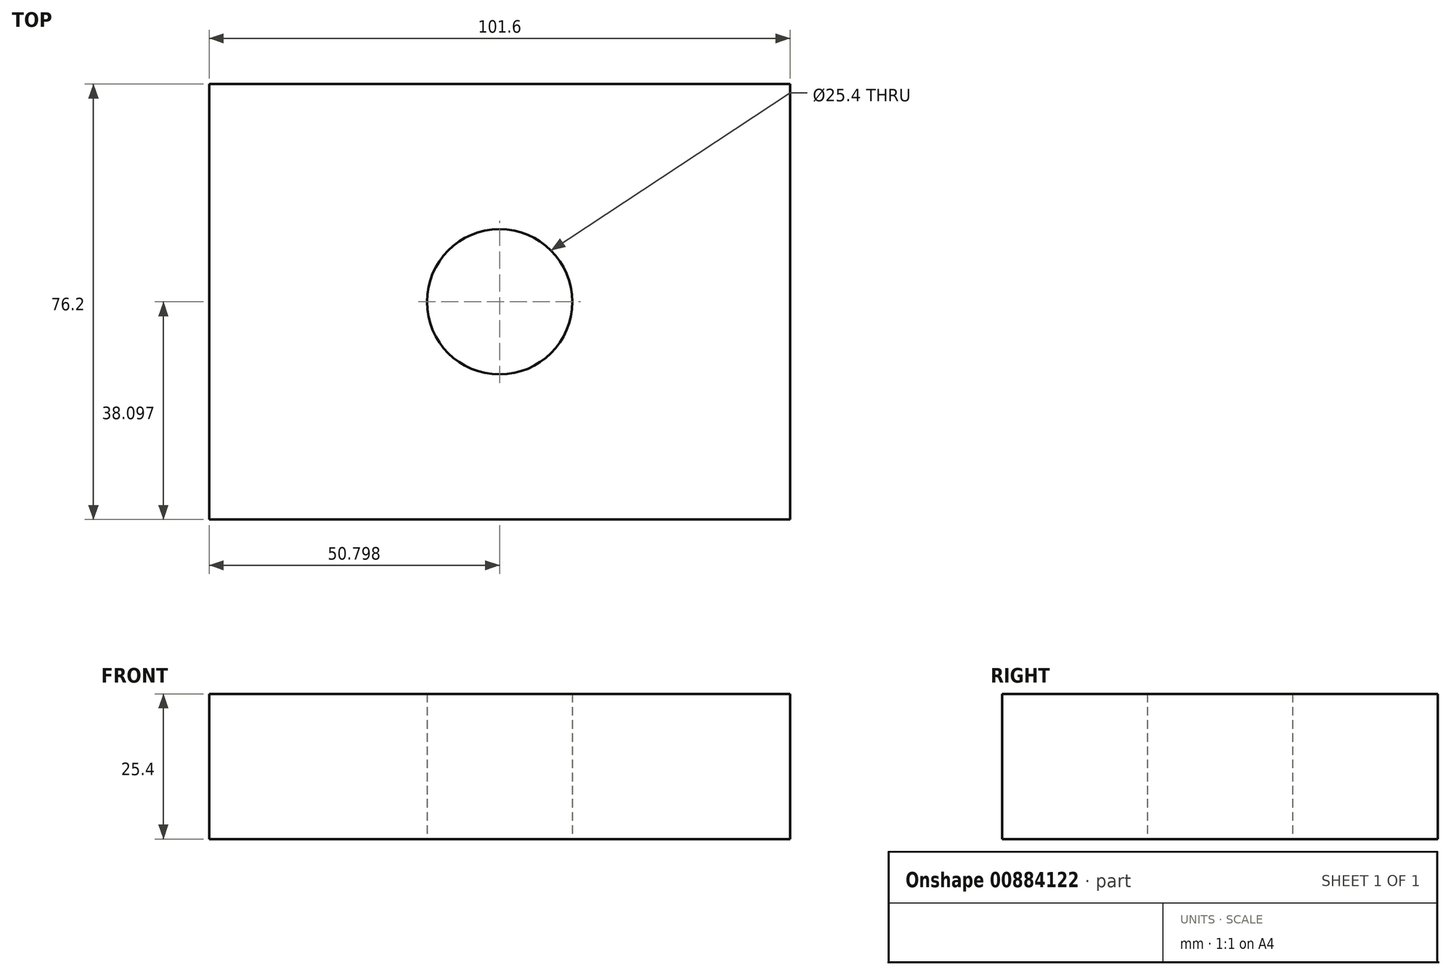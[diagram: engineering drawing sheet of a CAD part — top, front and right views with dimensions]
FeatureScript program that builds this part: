
annotation { "Feature Type Name" : "Feature", "Feature Type Description" : "" }
export const myFeature = defineFeature(function(context is Context, id is Id, definition is map)
    precondition{}
    {
        {
            var Q0;
            Q0=qCreatedBy(makeId("Top.planeOp"),FACE);
            var sketch = newSketch(context, id + "F0", { "sketchPlane" : qUnion([Q0])});
            skLineSegment(sketch, "E0.bottom", {"start": v(58.3, 44.06) * mm, "end": v(-43.3, 44.06) * mm});
            skLineSegment(sketch, "E0.top", {"start": v(58.3, -32.14) * mm, "end": v(-43.3, -32.14) * mm});
            skLineSegment(sketch, "E0.left", {"start": v(58.3, 44.06) * mm, "end": v(58.3, -32.14) * mm});
            skLineSegment(sketch, "E0.right", {"start": v(-43.3, 44.06) * mm, "end": v(-43.3, -32.14) * mm});
            skCircle(sketch, "E1", {"center": v(7.5, 5.96) * mm, "radius": 12.7 * mm});
            skSolve(sketch);
        }
        {
            var Q0;
            Q0=makeQuery(id+"F0.imprint","IMPRINT",FACE,{"disambiguationData":[TD([[makeQuery(id+"F0.imprint","IMPRINT",EDGE,{"derivedFrom":sQuery(id+"F0.wireOp",EDGE,"E0.bottom")}),1.0]])]});
            extrude(context, id + "F1", {"entities" : qUnion([Q0]), "depth" : 25.4 * mm, "offsetDistance" : 25.4 * mm});
        }
        {
            var Q0;
            Q0=makeQuery(id+"F1.opExtrude","CAP_FACE",FACE,{"disambiguationData":[OSD([sQuery(id+"F0.wireOp",EDGE,"E0.bottom"),sQuery(id+"F0.wireOp",EDGE,"E0.top"),sQuery(id+"F0.wireOp",EDGE,"E0.left"),sQuery(id+"F0.wireOp",EDGE,"E0.right")])],"isStart":false});
            var Q1;
            Q1=makeQuery(id+"F1.opExtrude","CAP_FACE",FACE,{"disambiguationData":[OSD([sQuery(id+"F0.wireOp",EDGE,"E0.bottom"),sQuery(id+"F0.wireOp",EDGE,"E0.top"),sQuery(id+"F0.wireOp",EDGE,"E0.left"),sQuery(id+"F0.wireOp",EDGE,"E0.right")])],"isStart":true});
            var Q2;
            Q2=makeQuery(id+"F1.opExtrude","SWEPT_FACE",FACE,{"disambiguationData":[OSD([sQuery(id+"F0.wireOp",EDGE,"E0.bottom")])]});
            var Q3;
            Q3=makeQuery(id+"F1.opExtrude","SWEPT_FACE",FACE,{"disambiguationData":[OSD([sQuery(id+"F0.wireOp",EDGE,"E0.top")])]});
            fillet(context, id + "F2", {"entities" : qUnion([Q0, Q1, Q2, Q3]), "radius" : 3.17 * mm, "tangentPropagation" : true, "allowEdgeOverflow" : false});
        }
        {
            var Q0;
            Q0=makeQuery(id+"F1.opExtrude","SWEPT_BODY",BODY,{"disambiguationData":[OSD([sQuery(id+"F0.wireOp",EDGE,"E0.bottom"),sQuery(id+"F0.wireOp",EDGE,"E0.top"),sQuery(id+"F0.wireOp",EDGE,"E0.left"),sQuery(id+"F0.wireOp",EDGE,"E0.right"),sQuery(id+"F0.wireOp",EDGE,"E1")])]});
            deleteBodies(context, id + "F3", {"entities" : qUnion([Q0])});
        }
        {
            var Q0;
            Q0=makeQuery(id+"F0.imprint","IMPRINT",FACE,{"disambiguationData":[TD([[makeQuery(id+"F0.imprint","IMPRINT",EDGE,{"derivedFrom":sQuery(id+"F0.wireOp",EDGE,"E0.bottom")}),1.0]])]});
            extrude(context, id + "F4", {"entities" : qUnion([Q0]), "depth" : 25.4 * mm, "offsetDistance" : 25.4 * mm});
        }
    });
